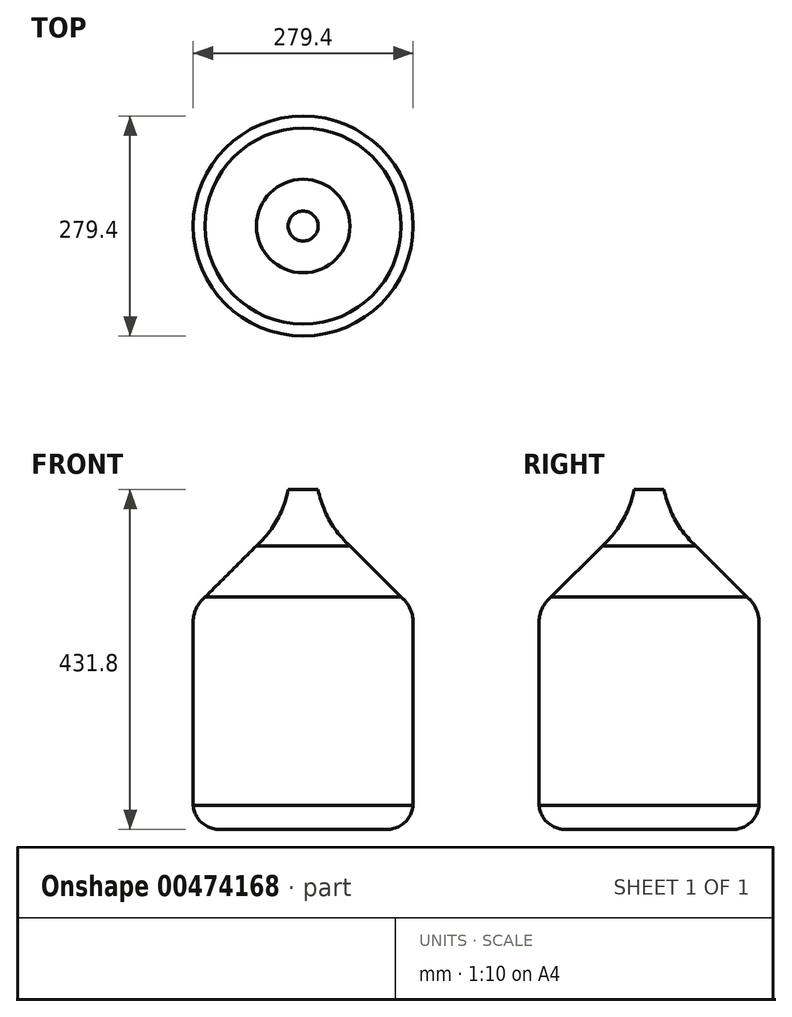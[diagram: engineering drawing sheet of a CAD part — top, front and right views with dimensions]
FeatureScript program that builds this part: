
annotation { "Feature Type Name" : "Feature", "Feature Type Description" : "" }
export const myFeature = defineFeature(function(context is Context, id is Id, definition is map)
    precondition{}
    {
        {
            var Q0;
            Q0=qCreatedBy(makeId("Front.planeOp"),FACE);
            var sketch = newSketch(context, id + "F0", { "sketchPlane" : qUnion([Q0])});
            skLineSegment(sketch, "E0", {"start": v(0, 0) * mm, "end": v(-106.42, 0) * mm});
            skArc(sketch, "E1", {"start": v(-139.7, 30.67) * mm, "mid": v(-129.05, 8.84) * mm, "end": v(-106.42, 0) * mm});
            skLineSegment(sketch, "E2", {"start": v(-139.7, 30.67) * mm, "end": v(-139.7, 263.33) * mm});
            skArc(sketch, "E3", {"start": v(-124.46, 295.17) * mm, "mid": v(-135.7, 280.98) * mm, "end": v(-139.7, 263.33) * mm});
            skLineSegment(sketch, "E4", {"start": v(-124.46, 295.17) * mm, "end": v(-59.38, 360.25) * mm});
            skArc(sketch, "E5", {"start": v(-59.38, 360.25) * mm, "mid": v(-33.37, 392.74) * mm, "end": v(-19.05, 431.8) * mm});
            skLineSegment(sketch, "E6", {"start": v(-19.05, 431.8) * mm, "end": v(0, 431.8) * mm});
            skLineSegment(sketch, "E7", {"start": v(0, 0) * mm, "end": v(0, 431.8) * mm});
            skSolve(sketch);
        }
        {
            var Q0;
            Q0 = qSketchRegion(id + "F0", true);
            var Q1;
            Q1=sQuery(id+"F0.wireOp",EDGE,"E7");
            revolve(context, id + "F1", {"entities" : qUnion([Q0]), "axis" : qUnion([Q1]), "revolveType" : RevolveType.FULL});
        }
    });
